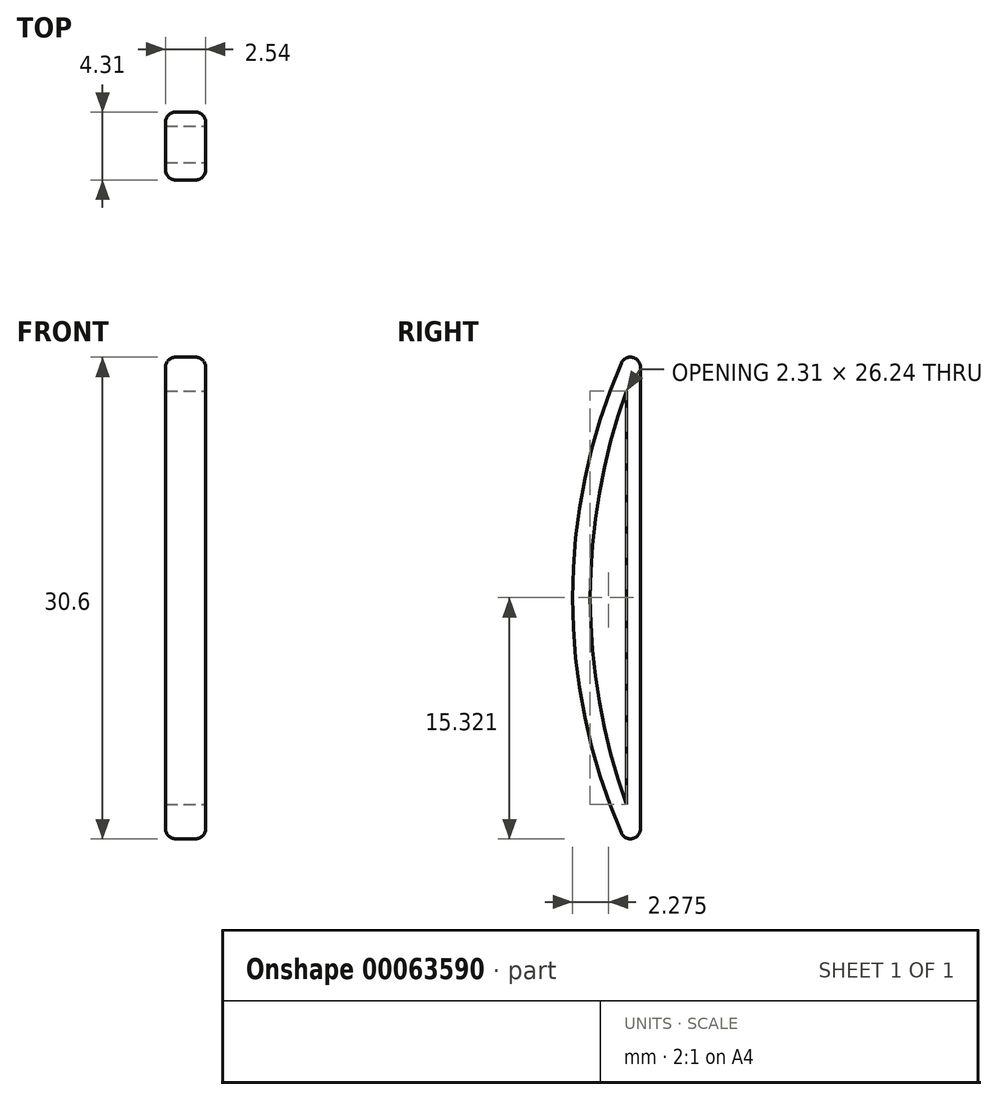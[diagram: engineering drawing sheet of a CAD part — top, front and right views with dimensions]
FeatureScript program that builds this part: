
annotation { "Feature Type Name" : "Feature", "Feature Type Description" : "" }
export const myFeature = defineFeature(function(context is Context, id is Id, definition is map)
    precondition{}
    {
        {
            var Q0;
            Q0=qCreatedBy(makeId("Right.planeOp"),FACE);
            var sketch = newSketch(context, id + "F0", { "sketchPlane" : qUnion([Q0])});
            skArc(sketch, "E0", {"start": v(0, 34.92) * mm, "mid": v(-4.3, 17.46) * mm, "end": v(0, 0) * mm});
            skLineSegment(sketch, "E1", {"start": v(0, 34.92) * mm, "end": v(0, 0) * mm});
            skSolve(sketch);
        }
        {
            var Q0;
            Q0=makeQuery(id+"F0.imprint","IMPRINT",FACE,{"disambiguationData":[TD([[makeQuery(id+"F0.imprint","IMPRINT",EDGE,{"derivedFrom":sQuery(id+"F0.wireOp",EDGE,"E0")}),1.0]])]});
            extrude(context, id + "F1", {"entities" : qUnion([Q0]), "depth" : 2.54 * mm});
        }
        {
            var Q0;
            Q0=makeQuery(id+"F1.opExtrude","CAP_FACE",FACE,{"disambiguationData":[OSD([sQuery(id+"F0.wireOp",EDGE,"E0"),sQuery(id+"F0.wireOp",EDGE,"E1")])],"isStart":false});
            var sketch = newSketch(context, id + "F2", { "sketchPlane" : qUnion([Q0])});
            skLineSegment(sketch, "E2", {"start": v(-0.88, 30.6) * mm, "end": v(-0.88, 4.36) * mm});
            skArc(sketch, "E3", {"start": v(-0.88, 30.6) * mm, "mid": v(-3.2, 17.48) * mm, "end": v(-0.88, 4.36) * mm});
            skSolve(sketch);
        }
        {
            var Q0;
            Q0=makeQuery(id+"F2.imprint","IMPRINT",FACE,{"disambiguationData":[TD([[makeQuery(id+"F2.imprint","IMPRINT",EDGE,{"derivedFrom":sQuery(id+"F2.wireOp",EDGE,"E2")}),-1.0]])]});
            extrude(context, id + "F3", {"entities" : qUnion([Q0]), "operationType" : NewBodyOperationType.REMOVE, "oppositeDirection" : true, "depth" : 25.4 * mm});
        }
        {
            var Q0;
            {var subQ0=sQuery(id+"F0.wireOp",EDGE,"E1");var subQ1=sQuery(id+"F0.wireOp",EDGE,"E0");Q0=makeQuery(id+"F1.opExtrude","SWEPT_EDGE",EDGE,{"disambiguationData":[OSD([subQ1,subQ0]),TDD([makeQuery(id+"F0.imprint","INTERSECT",VERTEX,{"disambiguationData":[OD(0.0)],"derivedFrom":[subQ1,subQ0]})])]});}
            var Q1;
            {var subQ0=sQuery(id+"F0.wireOp",EDGE,"E1");var subQ1=sQuery(id+"F0.wireOp",EDGE,"E0");Q1=makeQuery(id+"F1.opExtrude","SWEPT_EDGE",EDGE,{"disambiguationData":[OSD([subQ1,subQ0]),TDD([makeQuery(id+"F0.imprint","INTERSECT",VERTEX,{"disambiguationData":[OD(1.0)],"derivedFrom":[subQ1,subQ0]})])]});}
            fillet(context, id + "F4", {"entities" : qUnion([Q0, Q1]), "radius" : 0.64 * mm, "tangentPropagation" : true, "allowEdgeOverflow" : false});
        }
        {
            var Q0;
            Q0=makeQuery(id+"F1.opExtrude","CAP_EDGE",EDGE,{"disambiguationData":[OSD([sQuery(id+"F0.wireOp",EDGE,"E0")])],"isStart":true});
            fillet(context, id + "F5", {"entities" : qUnion([Q0]), "radius" : 0.64 * mm, "tangentPropagation" : true, "allowEdgeOverflow" : false});
        }
        {
            var Q0;
            Q0=makeQuery(id+"F1.opExtrude","CAP_EDGE",EDGE,{"disambiguationData":[OSD([sQuery(id+"F0.wireOp",EDGE,"E0")])],"isStart":false});
            fillet(context, id + "F6", {"entities" : qUnion([Q0]), "radius" : 0.64 * mm, "tangentPropagation" : true, "allowEdgeOverflow" : false});
        }
    });
